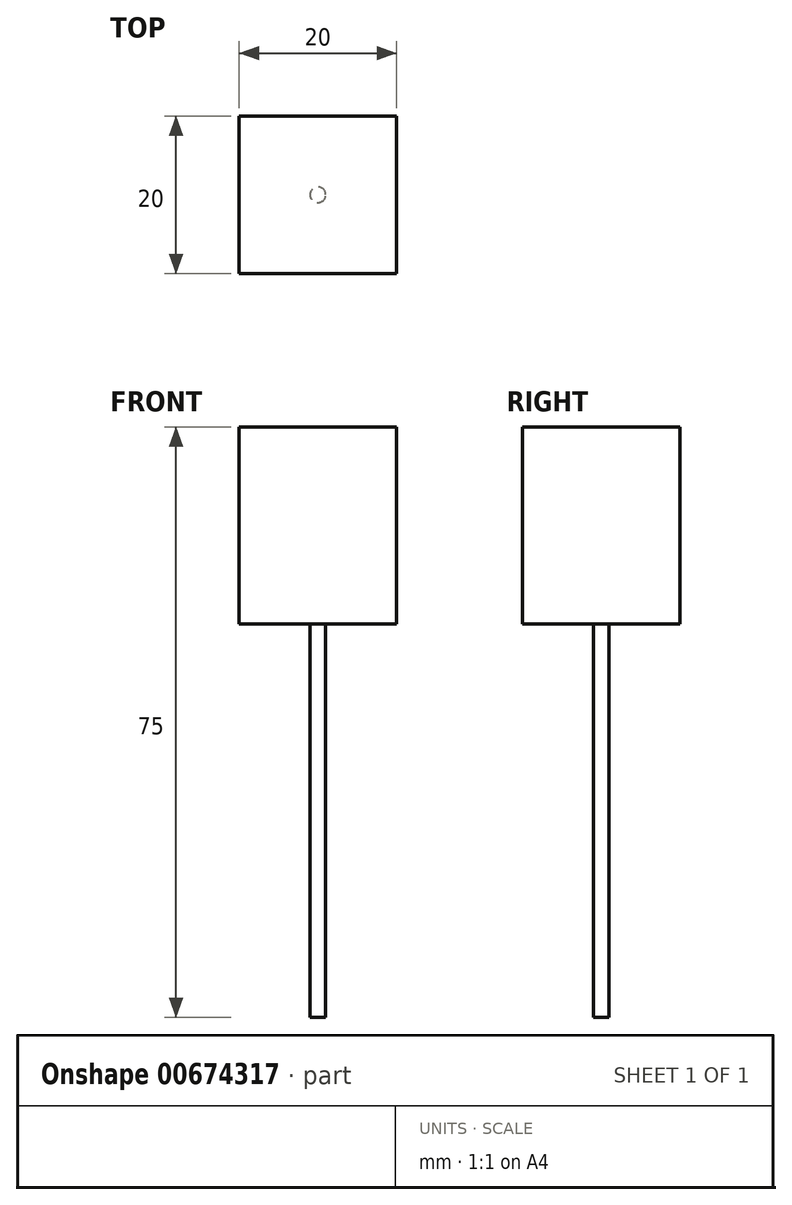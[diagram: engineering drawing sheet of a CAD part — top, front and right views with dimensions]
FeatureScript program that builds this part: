
annotation { "Feature Type Name" : "Feature", "Feature Type Description" : "" }
export const myFeature = defineFeature(function(context is Context, id is Id, definition is map)
    precondition{}
    {
        {
            var Q0;
            Q0=qCreatedBy(makeId("Top.planeOp"),FACE);
            var sketch = newSketch(context, id + "F0", { "sketchPlane" : qUnion([Q0])});
            skLineSegment(sketch, "E0.bottom", {"start": v(0, 0) * mm, "end": v(20, 0) * mm});
            skLineSegment(sketch, "E0.top", {"start": v(0, -20) * mm, "end": v(20, -20) * mm});
            skLineSegment(sketch, "E0.left", {"start": v(0, 0) * mm, "end": v(0, -20) * mm});
            skLineSegment(sketch, "E0.right", {"start": v(20, 0) * mm, "end": v(20, -20) * mm});
            skSolve(sketch);
        }
        {
            var Q0;
            Q0=makeQuery(id+"F0.imprint","IMPRINT",FACE,{"disambiguationData":[TD([[makeQuery(id+"F0.imprint","IMPRINT",EDGE,{"derivedFrom":sQuery(id+"F0.wireOp",EDGE,"E0.bottom")}),-1.0]])]});
            extrude(context, id + "F1", {"entities" : qUnion([Q0]), "depth" : 25 * mm, "offsetDistance" : 25 * mm});
        }
        {
            var Q0;
            Q0=makeQuery(id+"F1.opExtrude","CAP_FACE",FACE,{"disambiguationData":[OSD([sQuery(id+"F0.wireOp",EDGE,"E0.bottom"),sQuery(id+"F0.wireOp",EDGE,"E0.top"),sQuery(id+"F0.wireOp",EDGE,"E0.left"),sQuery(id+"F0.wireOp",EDGE,"E0.right")])],"isStart":true});
            var sketch = newSketch(context, id + "F2", { "sketchPlane" : qUnion([Q0])});
            skCircle(sketch, "E1", {"center": v(10, 10) * mm, "radius": 1 * mm});
            skSolve(sketch);
        }
        {
            var Q0;
            Q0 = qSketchRegion(id + "F2", true);
            extrude(context, id + "F3", {"entities" : qUnion([Q0]), "operationType" : NewBodyOperationType.ADD, "depth" : 50 * mm, "offsetDistance" : 25 * mm});
        }
    });
